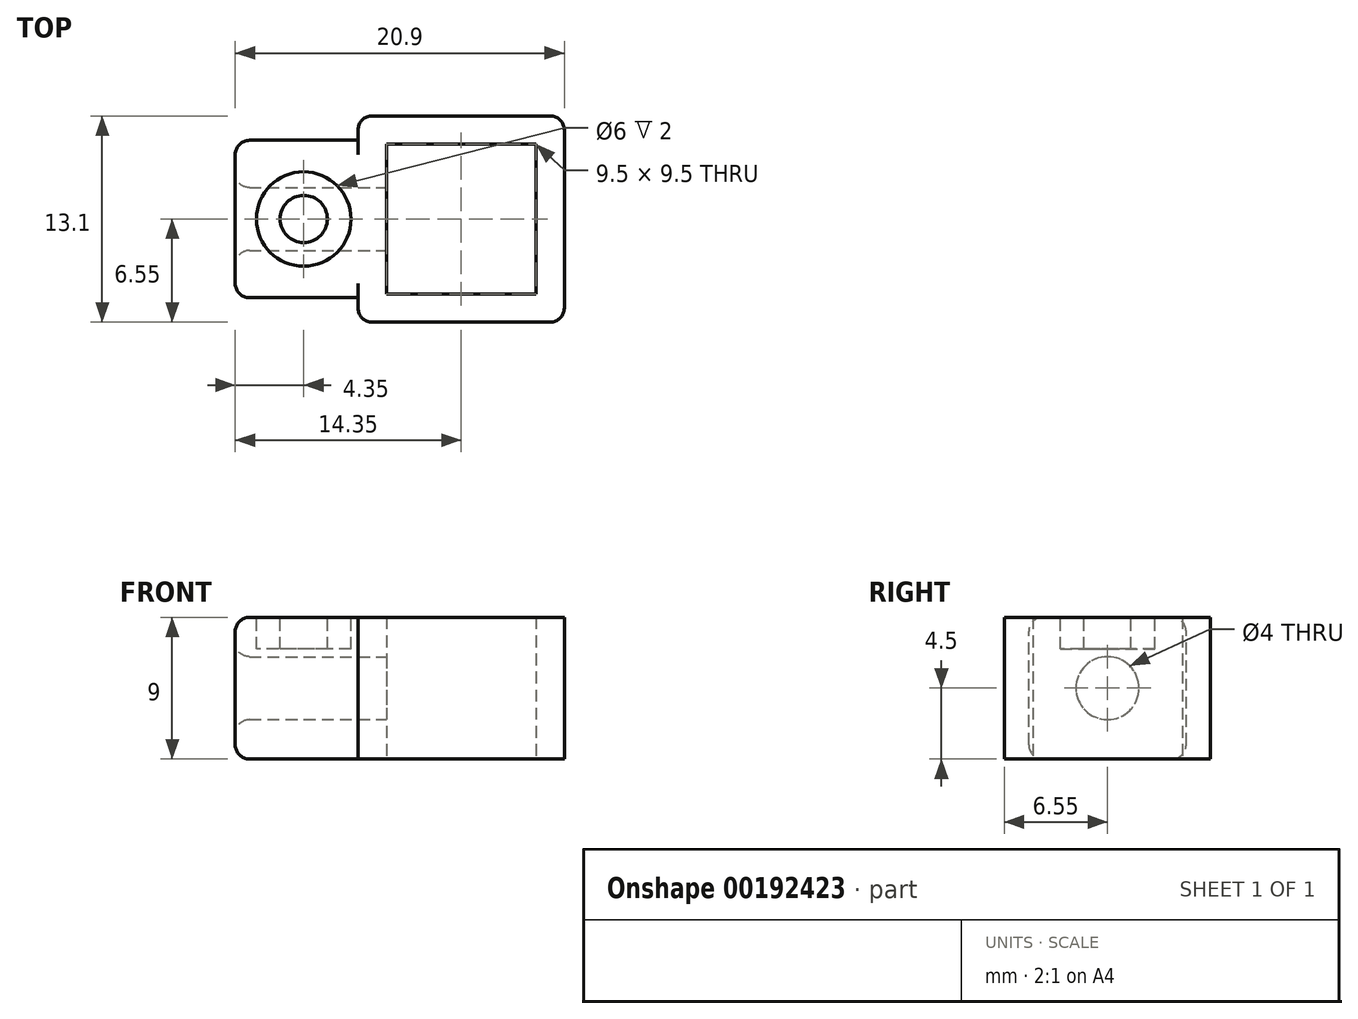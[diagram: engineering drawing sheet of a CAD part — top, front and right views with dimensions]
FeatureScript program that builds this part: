
annotation { "Feature Type Name" : "Feature", "Feature Type Description" : "" }
export const myFeature = defineFeature(function(context is Context, id is Id, definition is map)
    precondition{}
    {
        {
            var Q0;
            Q0=qCreatedBy(makeId("Top.planeOp"),FACE);
            var sketch = newSketch(context, id + "F0", { "sketchPlane" : qUnion([Q0])});
            skLineSegment(sketch, "E0.bottom", {"start": v(4.75, -4.75) * mm, "end": v(-4.75, -4.75) * mm});
            skLineSegment(sketch, "E0.top", {"start": v(4.75, 4.75) * mm, "end": v(-4.75, 4.75) * mm});
            skLineSegment(sketch, "E0.left", {"start": v(4.75, -4.75) * mm, "end": v(4.75, 4.75) * mm});
            skLineSegment(sketch, "E0.right", {"start": v(-4.75, -4.75) * mm, "end": v(-4.75, 4.75) * mm});
            skPoint(sketch, "E0.middle", {"position": v(0, 0) * mm});
            skLineSegment(sketch, "E1.0", {"start": v(6.55, 6.55) * mm, "end": v(-6.55, 6.55) * mm});
            skLineSegment(sketch, "E1.1", {"start": v(6.55, -6.55) * mm, "end": v(6.55, 6.55) * mm});
            skLineSegment(sketch, "E1.2", {"start": v(6.55, -6.55) * mm, "end": v(-6.55, -6.55) * mm});
            skLineSegment(sketch, "E1.3", {"start": v(-6.55, -6.55) * mm, "end": v(-6.55, 6.55) * mm});
            skSolve(sketch);
        }
        {
            var Q0;
            Q0=makeQuery(id+"F0.imprint","IMPRINT",FACE,{"disambiguationData":[TD([[makeQuery(id+"F0.imprint","IMPRINT",EDGE,{"derivedFrom":sQuery(id+"F0.wireOp",EDGE,"E0.bottom")}),1.0]])]});
            extrude(context, id + "F1", {"entities" : qUnion([Q0]), "depth" : 9 * mm});
        }
        {
            var Q0;
            Q0=qCreatedBy(makeId("Front.planeOp"),FACE);
            var sketch = newSketch(context, id + "F2", { "sketchPlane" : qUnion([Q0])});
            skLineSegment(sketch, "E2", {"start": v(0, 0) * mm, "end": v(0, 4.5) * mm});
            skLineSegment(sketch, "E3", {"start": v(0, 4.5) * mm, "end": v(-6.55, 4.5) * mm});
            skLineSegment(sketch, "E4", {"start": v(-6.55, 4.5) * mm, "end": v(-9.55, 4.5) * mm});
            skLineSegment(sketch, "E5", {"start": v(-9.55, 4.5) * mm, "end": v(-9.55, 6.77) * mm});
            skLineSegment(sketch, "E6", {"start": v(-9.55, 6.77) * mm, "end": v(-11.05, 6.77) * mm});
            skLineSegment(sketch, "E7", {"start": v(-11.05, 6.77) * mm, "end": v(-11.05, 4.5) * mm});
            skLineSegment(sketch, "E8", {"start": v(-11.05, 4.5) * mm, "end": v(-12.85, 4.5) * mm});
            skLineSegment(sketch, "E9", {"start": v(-12.85, 4.5) * mm, "end": v(-12.85, 6.77) * mm});
            skLineSegment(sketch, "E10", {"start": v(-12.85, 6.77) * mm, "end": v(-14.35, 6.77) * mm});
            skLineSegment(sketch, "E11", {"start": v(-14.35, 6.77) * mm, "end": v(-14.35, 2.97) * mm});
            skLineSegment(sketch, "E12", {"start": v(-14.35, 2.97) * mm, "end": v(-6.55, 0) * mm});
            skLineSegment(sketch, "E13", {"start": v(-6.55, 4.5) * mm, "end": v(-6.55, 0) * mm});
            skLineSegment(sketch, "E14", {"start": v(-6.55, 0) * mm, "end": v(-14.35, 0) * mm});
            skLineSegment(sketch, "E15", {"start": v(-14.35, 0) * mm, "end": v(-14.35, 2.97) * mm});
            skLineSegment(sketch, "E16", {"start": v(-6.55, 4.5) * mm, "end": v(-6.55, 9) * mm});
            skLineSegment(sketch, "E17", {"start": v(-6.55, 9) * mm, "end": v(-14.35, 9) * mm});
            skLineSegment(sketch, "E18", {"start": v(-14.35, 9) * mm, "end": v(-14.35, 6.77) * mm});
            skSolve(sketch);
        }
        {
            var Q0;
            Q0=qSketchRegion(id+"F2",true);
            extrude(context, id + "F3", {"entities" : qUnion([Q0]), "operationType" : NewBodyOperationType.ADD, "endBound" : BoundingType.SYMMETRIC, "depth" : 10 * mm});
        }
        {
            var Q0;
            Q0=makeQuery(id+"F3.boolean.opBoolean","MERGE",FACE,{"derivedFrom":[makeQuery(id+"F1.opExtrude","CAP_FACE",FACE,{"disambiguationData":[OSD([sQuery(id+"F0.wireOp",EDGE,"E0.bottom"),sQuery(id+"F0.wireOp",EDGE,"E0.top"),sQuery(id+"F0.wireOp",EDGE,"E0.left"),sQuery(id+"F0.wireOp",EDGE,"E0.right"),sQuery(id+"F0.wireOp",EDGE,"E1.0"),sQuery(id+"F0.wireOp",EDGE,"E1.1"),sQuery(id+"F0.wireOp",EDGE,"E1.2"),sQuery(id+"F0.wireOp",EDGE,"E1.3")])],"isStart":false}),makeQuery(id+"F3.opExtrude","SWEPT_FACE",FACE,{"disambiguationData":[OSD([sQuery(id+"F2.wireOp",EDGE,"E17")])]})]});
            cPlane(context, id + "F4", {"entities" : qUnion([Q0]), "cplaneType" : CPlaneType.OFFSET, "offset" : 0 * mm, "width" : 150 * mm, "height" : 150 * mm});
        }
        {
            var Q0;
            Q0=qCreatedBy(id+"F4.planeOp",FACE);
            var sketch = newSketch(context, id + "F5", { "sketchPlane" : qUnion([Q0])});
            skLineSegment(sketch, "E19", {"start": v(0, 0) * mm, "end": v(-10, 0) * mm});
            skCircle(sketch, "E20", {"center": v(-10, 0) * mm, "radius": 1.5 * mm});
            skCircle(sketch, "E21", {"center": v(-10, 0) * mm, "radius": 3 * mm});
            skSolve(sketch);
        }
        {
            var Q0;
            Q0 = qSketchRegion(id + "F5", true);
            extrude(context, id + "F6", {"entities" : qUnion([Q0]), "operationType" : NewBodyOperationType.REMOVE, "oppositeDirection" : true, "depth" : 2 * mm});
        }
        {
            var Q0;
            Q0=qCreatedBy(makeId("Right.planeOp"),FACE);
            var sketch = newSketch(context, id + "F7", { "sketchPlane" : qUnion([Q0])});
            skLineSegment(sketch, "E22", {"start": v(0, 0) * mm, "end": v(0, 4.5) * mm});
            skCircle(sketch, "E23", {"center": v(0, 4.5) * mm, "radius": 2 * mm});
            skSolve(sketch);
        }
        {
            var Q0;
            Q0 = qSketchRegion(id + "F7", true);
            extrude(context, id + "F8", {"entities" : qUnion([Q0]), "operationType" : NewBodyOperationType.REMOVE, "oppositeDirection" : true, "depth" : 25 * mm});
        }
        {
            var Q0;
            Q0=makeQuery(id+"F3.opExtrude","SWEPT_FACE",FACE,{"disambiguationData":[OSD([sQuery(id+"F2.wireOp",EDGE,"E11"),sQuery(id+"F2.wireOp",EDGE,"E15"),sQuery(id+"F2.wireOp",EDGE,"E18")])]});
            var Q1;
            Q1=makeQuery(id+"F1.opExtrude","SWEPT_EDGE",EDGE,{"disambiguationData":[OSD([sQuery(id+"F0.wireOp",EDGE,"E1.0"),sQuery(id+"F0.wireOp",EDGE,"E1.3")])]});
            var Q2;
            Q2=makeQuery(id+"F1.opExtrude","SWEPT_EDGE",EDGE,{"disambiguationData":[OSD([sQuery(id+"F0.wireOp",EDGE,"E1.0"),sQuery(id+"F0.wireOp",EDGE,"E1.1")])]});
            var Q3;
            Q3=makeQuery(id+"F1.opExtrude","SWEPT_EDGE",EDGE,{"disambiguationData":[OSD([sQuery(id+"F0.wireOp",EDGE,"E1.2"),sQuery(id+"F0.wireOp",EDGE,"E1.3")])]});
            var Q4;
            Q4=makeQuery(id+"F3.opExtrude","CAP_EDGE",EDGE,{"disambiguationData":[OSD([sQuery(id+"F2.wireOp",EDGE,"E17")])],"isStart":true});
            var Q5;
            Q5=makeQuery(id+"F3.opExtrude","CAP_EDGE",EDGE,{"disambiguationData":[OSD([sQuery(id+"F2.wireOp",EDGE,"E14")])],"isStart":true});
            var Q6;
            Q6=makeQuery(id+"F1.opExtrude","SWEPT_EDGE",EDGE,{"disambiguationData":[OSD([sQuery(id+"F0.wireOp",EDGE,"E1.1"),sQuery(id+"F0.wireOp",EDGE,"E1.2")])]});
            var Q7;
            Q7=makeQuery(id+"F3.opExtrude","CAP_EDGE",EDGE,{"disambiguationData":[OSD([sQuery(id+"F2.wireOp",EDGE,"E14")])],"isStart":false});
            var Q8;
            Q8=makeQuery(id+"F3.opExtrude","CAP_EDGE",EDGE,{"disambiguationData":[OSD([sQuery(id+"F2.wireOp",EDGE,"E17")])],"isStart":false});
            fillet(context, id + "F9", {"entities" : qUnion([Q0, Q1, Q2, Q3, Q4, Q5, Q6, Q7, Q8]), "radius" : 0.9 * mm, "tangentPropagation" : true, "allowEdgeOverflow" : false});
        }
    });
